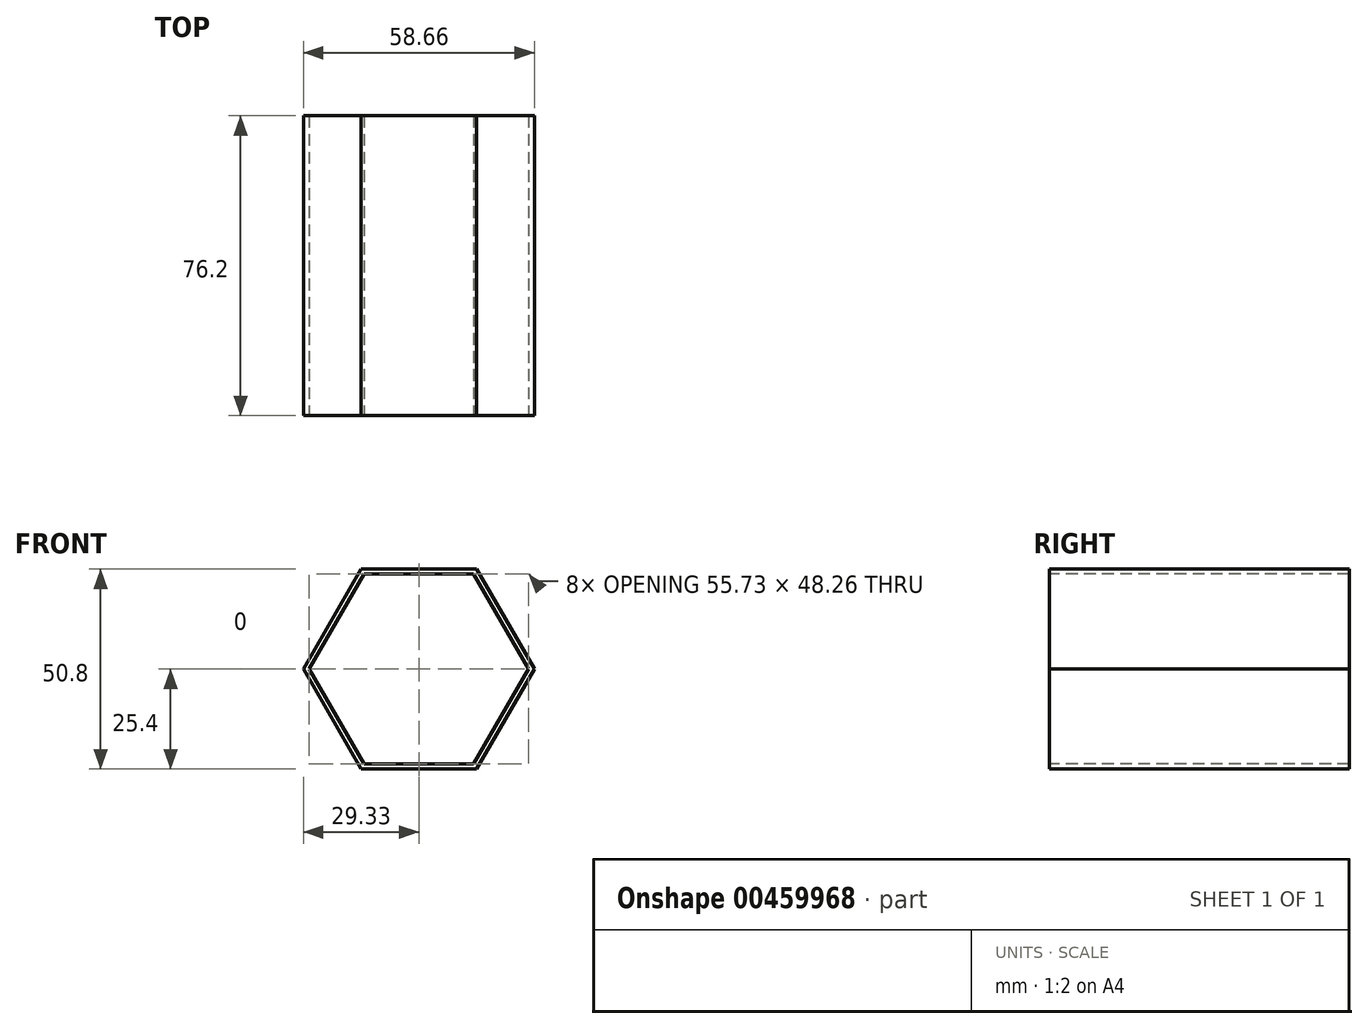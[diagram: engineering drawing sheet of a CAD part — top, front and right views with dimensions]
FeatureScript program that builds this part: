
annotation { "Feature Type Name" : "Feature", "Feature Type Description" : "" }
export const myFeature = defineFeature(function(context is Context, id is Id, definition is map)
    precondition{}
    {
        {
            var Q0;
            Q0=qCreatedBy(makeId("Front.planeOp"),FACE);
            var sketch = newSketch(context, id + "F0", { "sketchPlane" : qUnion([Q0])});
            skCircle(sketch, "E0.cCircle", {"center": v(0, 0) * mm, "radius": 25.4 * mm, "construction": true});
            skLineSegment(sketch, "E0.0", {"start": v(14.66, 25.4) * mm, "end": v(29.33, 0) * mm});
            skLineSegment(sketch, "E0.1", {"start": v(29.33, 0) * mm, "end": v(14.66, -25.4) * mm});
            skLineSegment(sketch, "E0.2", {"start": v(14.66, -25.4) * mm, "end": v(-14.66, -25.4) * mm});
            skLineSegment(sketch, "E0.3", {"start": v(-14.66, -25.4) * mm, "end": v(-29.33, 0) * mm});
            skLineSegment(sketch, "E0.4", {"start": v(-29.33, 0) * mm, "end": v(-14.66, 25.4) * mm});
            skLineSegment(sketch, "E0.5", {"start": v(-14.66, 25.4) * mm, "end": v(14.66, 25.4) * mm});
            skPoint(sketch, "E0.0.midPoint", {"position": v(22, 12.7) * mm});
            skLineSegment(sketch, "E1.0", {"start": v(-27.86, 0) * mm, "end": v(-13.93, 24.13) * mm});
            skLineSegment(sketch, "E1.1", {"start": v(13.93, 24.13) * mm, "end": v(27.86, 0) * mm});
            skLineSegment(sketch, "E1.2", {"start": v(27.86, 0) * mm, "end": v(13.93, -24.13) * mm});
            skLineSegment(sketch, "E1.3", {"start": v(-13.93, 24.13) * mm, "end": v(13.93, 24.13) * mm});
            skLineSegment(sketch, "E1.4", {"start": v(13.93, -24.13) * mm, "end": v(-13.93, -24.13) * mm});
            skLineSegment(sketch, "E1.5", {"start": v(-13.93, -24.13) * mm, "end": v(-27.86, 0) * mm});
            skSolve(sketch);
        }
        {
            var Q0;
            Q0 = qSketchRegion(id + "F0", true);
            extrude(context, id + "F1", {"entities" : qUnion([Q0]), "oppositeDirection" : true, "depth" : 76.2 * mm});
        }
    });
